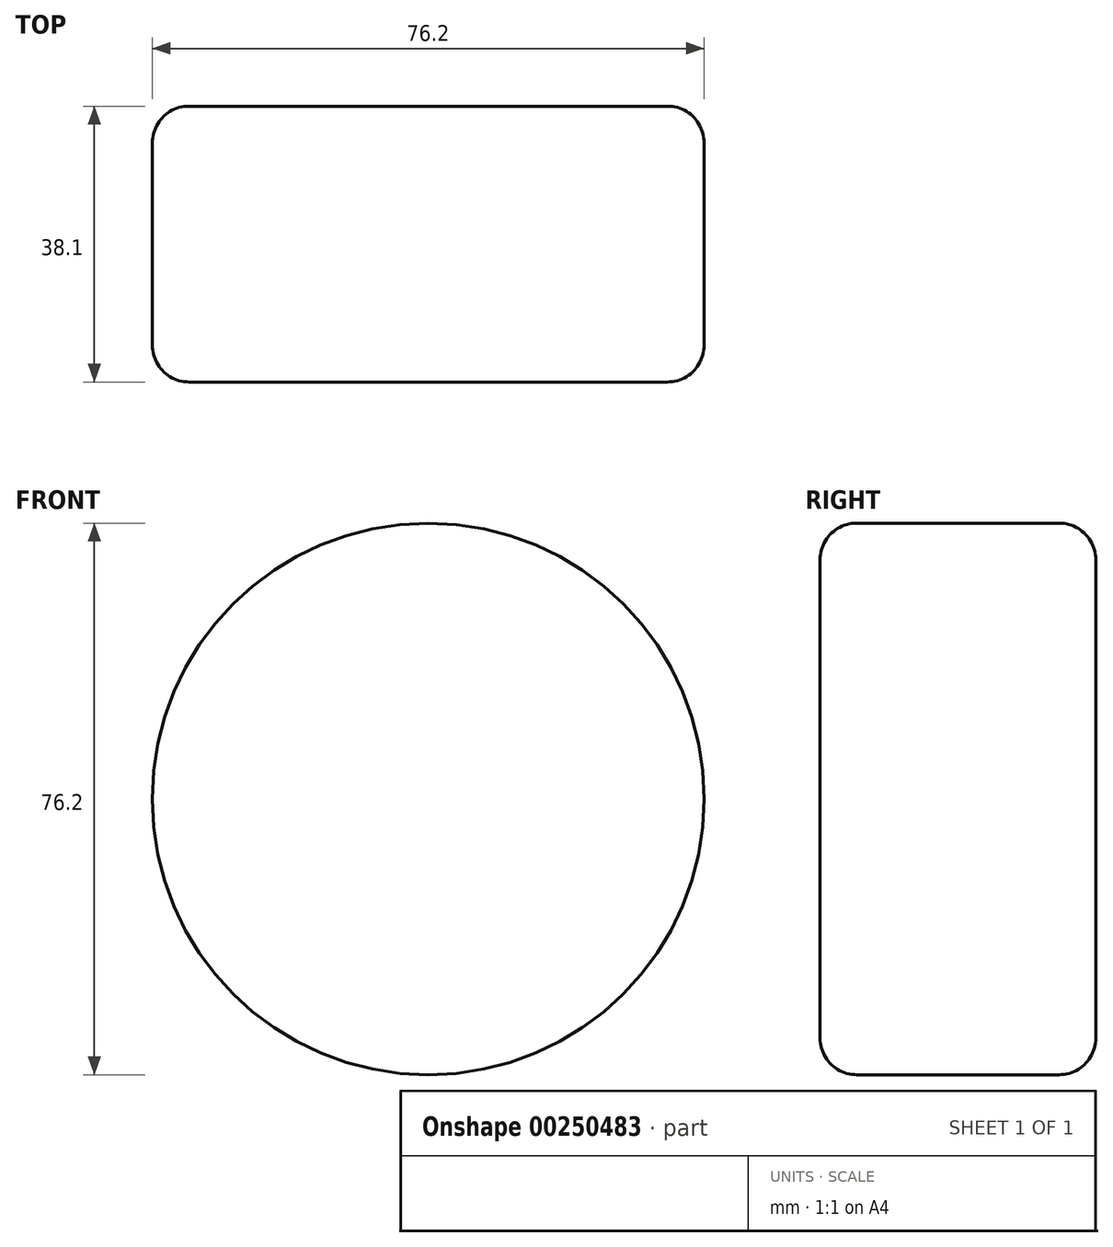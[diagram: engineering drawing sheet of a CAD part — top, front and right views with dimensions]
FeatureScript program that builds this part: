
annotation { "Feature Type Name" : "Feature", "Feature Type Description" : "" }
export const myFeature = defineFeature(function(context is Context, id is Id, definition is map)
    precondition{}
    {
        {
            var Q0;
            Q0=qCreatedBy(makeId("Front.planeOp"),FACE);
            var sketch = newSketch(context, id + "F0", { "sketchPlane" : qUnion([Q0])});
            skCircle(sketch, "E0", {"center": v(0, 0) * mm, "radius": 38.1 * mm});
            skSolve(sketch);
        }
        {
            var Q0;
            Q0=makeQuery(id+"F0.imprint","IMPRINT",FACE,{"disambiguationData":[TD([[makeQuery(id+"F0.imprint","IMPRINT",EDGE,{"derivedFrom":sQuery(id+"F0.wireOp",EDGE,"E0")}),1.0]])]});
            extrude(context, id + "F1", {"entities" : qUnion([Q0]), "depth" : 38.1 * mm});
        }
        {
            var Q0;
            Q0=makeQuery(id+"F1.opExtrude","CAP_FACE",FACE,{"disambiguationData":[OSD([sQuery(id+"F0.wireOp",EDGE,"E0")])],"isStart":false});
            var Q1;
            Q1=makeQuery(id+"F1.opExtrude","CAP_EDGE",EDGE,{"disambiguationData":[OSD([sQuery(id+"F0.wireOp",EDGE,"E0")])],"isStart":true});
            fillet(context, id + "F2", {"entities" : qUnion([Q0, Q1]), "radius" : 5.08 * mm, "tangentPropagation" : true, "allowEdgeOverflow" : false});
        }
    });
